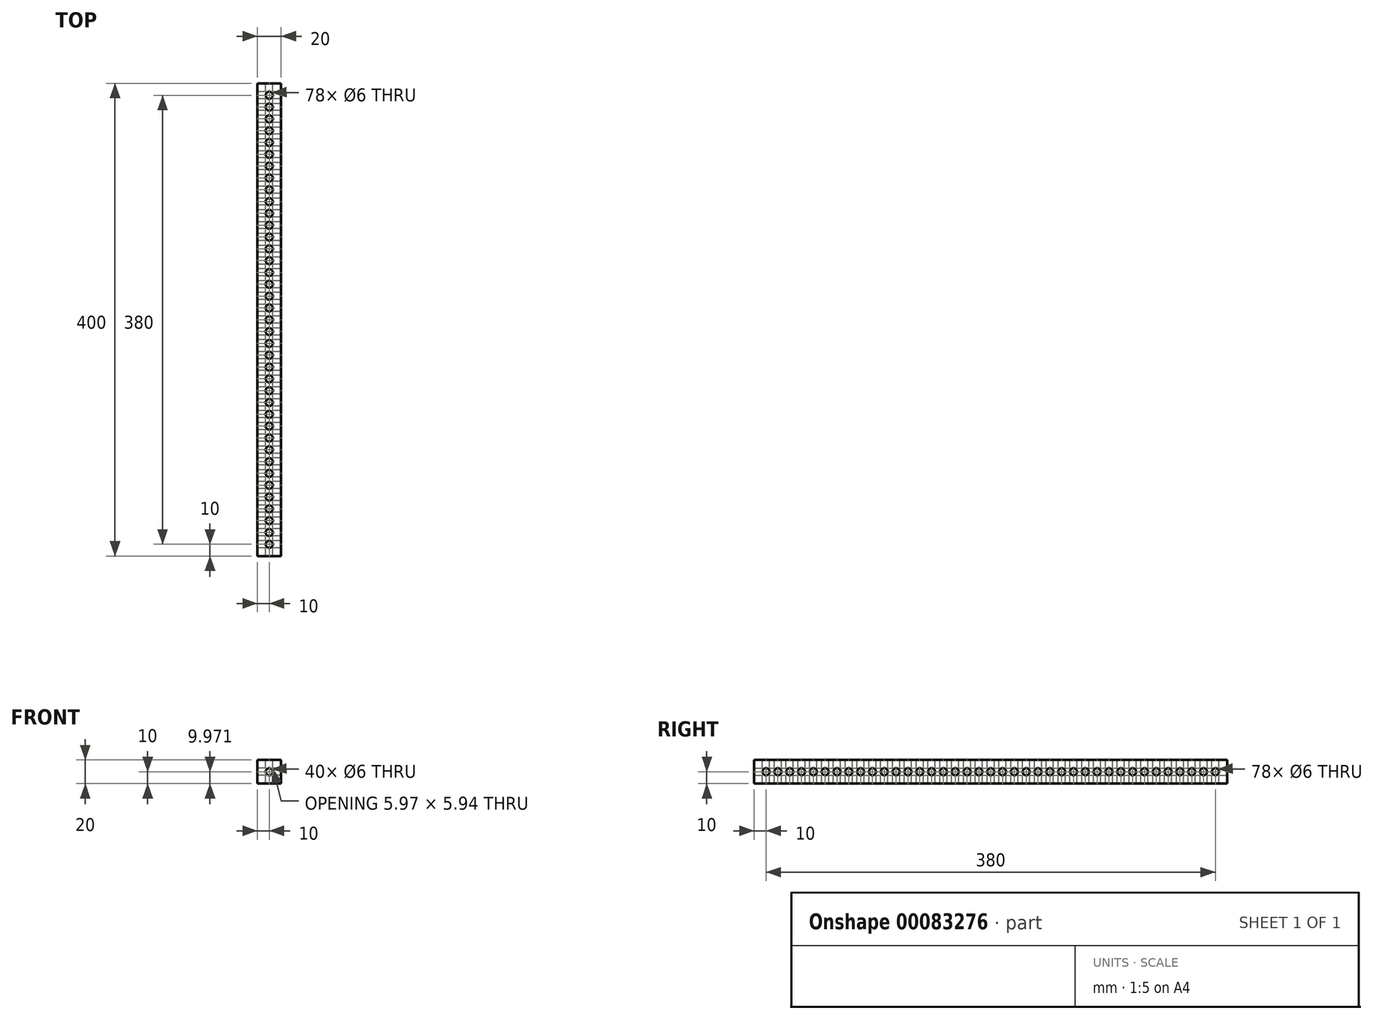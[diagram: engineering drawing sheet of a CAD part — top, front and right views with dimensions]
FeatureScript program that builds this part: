
annotation { "Feature Type Name" : "Feature", "Feature Type Description" : "" }
export const myFeature = defineFeature(function(context is Context, id is Id, definition is map)
    precondition{}
    {
        {
            var Q0;
            Q0=qCreatedBy(makeId("Front.planeOp"),FACE);
            var sketch = newSketch(context, id + "F0", { "sketchPlane" : qUnion([Q0])});
            skLineSegment(sketch, "E0.bottom", {"start": v(10, 10) * mm, "end": v(-10, 10) * mm});
            skLineSegment(sketch, "E0.top", {"start": v(10, -10) * mm, "end": v(-10, -10) * mm});
            skLineSegment(sketch, "E0.left", {"start": v(10, 10) * mm, "end": v(10, -10) * mm});
            skLineSegment(sketch, "E0.right", {"start": v(-10, 10) * mm, "end": v(-10, -10) * mm});
            skPoint(sketch, "E0.middle", {"position": v(0, 0) * mm});
            skCircle(sketch, "E1", {"center": v(0, 0) * mm, "radius": 3 * mm});
            skSolve(sketch);
        }
        {
            var Q0;
            Q0 = qSketchRegion(id + "F0", true);
            extrude(context, id + "F1", {"entities" : qUnion([Q0]), "depth" : 400 * mm});
        }
        {
            var Q0;
            Q0=makeQuery(id+"F1.opExtrude","SWEPT_FACE",FACE,{"disambiguationData":[OSD([sQuery(id+"F0.wireOp",EDGE,"E0.bottom")])]});
            var sketch = newSketch(context, id + "F2", { "sketchPlane" : qUnion([Q0])});
            skCircle(sketch, "E2", {"center": v(0, -10) * mm, "radius": 3 * mm});
            skCircle(sketch, "E3.0.1.0", {"center": v(0, -20) * mm, "radius": 3 * mm});
            skCircle(sketch, "E3.0.2.0", {"center": v(0, -30) * mm, "radius": 3 * mm});
            skCircle(sketch, "E3.0.3.0", {"center": v(0, -40) * mm, "radius": 3 * mm});
            skCircle(sketch, "E3.0.4.0", {"center": v(0, -50) * mm, "radius": 3 * mm});
            skCircle(sketch, "E3.0.5.0", {"center": v(0, -60) * mm, "radius": 3 * mm});
            skCircle(sketch, "E3.0.6.0", {"center": v(0, -70) * mm, "radius": 3 * mm});
            skCircle(sketch, "E3.0.7.0", {"center": v(0, -80) * mm, "radius": 3 * mm});
            skCircle(sketch, "E3.0.8.0", {"center": v(0, -90) * mm, "radius": 3 * mm});
            skCircle(sketch, "E3.0.9.0", {"center": v(0, -100) * mm, "radius": 3 * mm});
            skCircle(sketch, "E3.0.10.0", {"center": v(0, -110) * mm, "radius": 3 * mm});
            skCircle(sketch, "E3.0.11.0", {"center": v(0, -120) * mm, "radius": 3 * mm});
            skCircle(sketch, "E3.0.12.0", {"center": v(0, -130) * mm, "radius": 3 * mm});
            skCircle(sketch, "E3.0.13.0", {"center": v(0, -140) * mm, "radius": 3 * mm});
            skCircle(sketch, "E3.0.14.0", {"center": v(0, -150) * mm, "radius": 3 * mm});
            skCircle(sketch, "E3.0.15.0", {"center": v(0, -160) * mm, "radius": 3 * mm});
            skCircle(sketch, "E3.0.16.0", {"center": v(0, -170) * mm, "radius": 3 * mm});
            skCircle(sketch, "E3.0.17.0", {"center": v(0, -180) * mm, "radius": 3 * mm});
            skCircle(sketch, "E3.0.18.0", {"center": v(0, -190) * mm, "radius": 3 * mm});
            skCircle(sketch, "E3.0.19.0", {"center": v(0, -200) * mm, "radius": 3 * mm});
            skCircle(sketch, "E3.0.20.0", {"center": v(0, -210) * mm, "radius": 3 * mm});
            skCircle(sketch, "E3.0.21.0", {"center": v(0, -220) * mm, "radius": 3 * mm});
            skCircle(sketch, "E3.0.22.0", {"center": v(0, -230) * mm, "radius": 3 * mm});
            skCircle(sketch, "E3.0.23.0", {"center": v(0, -240) * mm, "radius": 3 * mm});
            skCircle(sketch, "E3.0.24.0", {"center": v(0, -250) * mm, "radius": 3 * mm});
            skCircle(sketch, "E3.0.25.0", {"center": v(0, -260) * mm, "radius": 3 * mm});
            skCircle(sketch, "E3.0.26.0", {"center": v(0, -270) * mm, "radius": 3 * mm});
            skCircle(sketch, "E3.0.27.0", {"center": v(0, -280) * mm, "radius": 3 * mm});
            skCircle(sketch, "E3.0.28.0", {"center": v(0, -290) * mm, "radius": 3 * mm});
            skCircle(sketch, "E3.0.29.0", {"center": v(0, -300) * mm, "radius": 3 * mm});
            skCircle(sketch, "E3.0.30.0", {"center": v(0, -310) * mm, "radius": 3 * mm});
            skCircle(sketch, "E3.0.31.0", {"center": v(0, -320) * mm, "radius": 3 * mm});
            skCircle(sketch, "E3.0.32.0", {"center": v(0, -330) * mm, "radius": 3 * mm});
            skCircle(sketch, "E3.0.33.0", {"center": v(0, -340) * mm, "radius": 3 * mm});
            skCircle(sketch, "E3.0.34.0", {"center": v(0, -350) * mm, "radius": 3 * mm});
            skCircle(sketch, "E3.0.35.0", {"center": v(0, -360) * mm, "radius": 3 * mm});
            skCircle(sketch, "E3.0.36.0", {"center": v(0, -370) * mm, "radius": 3 * mm});
            skCircle(sketch, "E3.0.37.0", {"center": v(0, -380) * mm, "radius": 3 * mm});
            skCircle(sketch, "E3.0.38.0", {"center": v(0, -390) * mm, "radius": 3 * mm});
            skLineSegment(sketch, "E3.direction1", {"start": v(0, -10) * mm, "end": v(25, -10) * mm, "construction": true});
            skLineSegment(sketch, "E3.direction2", {"start": v(0, -10) * mm, "end": v(0, -20) * mm, "construction": true});
            skSolve(sketch);
        }
        {
            var Q0;
            Q0 = qSketchRegion(id + "F2", true);
            extrude(context, id + "F3", {"entities" : qUnion([Q0]), "operationType" : NewBodyOperationType.REMOVE, "endBound" : BoundingType.THROUGH_ALL, "oppositeDirection" : true, "depth" : 25 * mm});
        }
        {
            var Q0;
            Q0=makeQuery(id+"F1.opExtrude","SWEPT_FACE",FACE,{"disambiguationData":[OSD([sQuery(id+"F0.wireOp",EDGE,"E0.right")])]});
            var sketch = newSketch(context, id + "F4", { "sketchPlane" : qUnion([Q0])});
            skCircle(sketch, "E4", {"center": v(10, 0) * mm, "radius": 3 * mm});
            skCircle(sketch, "E5.1.0.0", {"center": v(20, 0) * mm, "radius": 3 * mm});
            skCircle(sketch, "E5.2.0.0", {"center": v(30, 0) * mm, "radius": 3 * mm});
            skCircle(sketch, "E5.3.0.0", {"center": v(40, 0) * mm, "radius": 3 * mm});
            skCircle(sketch, "E5.4.0.0", {"center": v(50, 0) * mm, "radius": 3 * mm});
            skCircle(sketch, "E5.5.0.0", {"center": v(60, 0) * mm, "radius": 3 * mm});
            skCircle(sketch, "E5.6.0.0", {"center": v(70, 0) * mm, "radius": 3 * mm});
            skCircle(sketch, "E5.7.0.0", {"center": v(80, 0) * mm, "radius": 3 * mm});
            skCircle(sketch, "E5.8.0.0", {"center": v(90, 0) * mm, "radius": 3 * mm});
            skCircle(sketch, "E5.9.0.0", {"center": v(100, 0) * mm, "radius": 3 * mm});
            skCircle(sketch, "E5.10.0.0", {"center": v(110, 0) * mm, "radius": 3 * mm});
            skCircle(sketch, "E5.11.0.0", {"center": v(120, 0) * mm, "radius": 3 * mm});
            skCircle(sketch, "E5.12.0.0", {"center": v(130, 0) * mm, "radius": 3 * mm});
            skCircle(sketch, "E5.13.0.0", {"center": v(140, 0) * mm, "radius": 3 * mm});
            skCircle(sketch, "E5.14.0.0", {"center": v(150, 0) * mm, "radius": 3 * mm});
            skCircle(sketch, "E5.15.0.0", {"center": v(160, 0) * mm, "radius": 3 * mm});
            skCircle(sketch, "E5.16.0.0", {"center": v(170, 0) * mm, "radius": 3 * mm});
            skCircle(sketch, "E5.17.0.0", {"center": v(180, 0) * mm, "radius": 3 * mm});
            skCircle(sketch, "E5.18.0.0", {"center": v(190, 0) * mm, "radius": 3 * mm});
            skCircle(sketch, "E5.19.0.0", {"center": v(200, 0) * mm, "radius": 3 * mm});
            skCircle(sketch, "E5.20.0.0", {"center": v(210, 0) * mm, "radius": 3 * mm});
            skCircle(sketch, "E5.21.0.0", {"center": v(220, 0) * mm, "radius": 3 * mm});
            skCircle(sketch, "E5.22.0.0", {"center": v(230, 0) * mm, "radius": 3 * mm});
            skCircle(sketch, "E5.23.0.0", {"center": v(240, 0) * mm, "radius": 3 * mm});
            skCircle(sketch, "E5.24.0.0", {"center": v(250, 0) * mm, "radius": 3 * mm});
            skCircle(sketch, "E5.25.0.0", {"center": v(260, 0) * mm, "radius": 3 * mm});
            skCircle(sketch, "E5.26.0.0", {"center": v(270, 0) * mm, "radius": 3 * mm});
            skCircle(sketch, "E5.27.0.0", {"center": v(280, 0) * mm, "radius": 3 * mm});
            skCircle(sketch, "E5.28.0.0", {"center": v(290, 0) * mm, "radius": 3 * mm});
            skCircle(sketch, "E5.29.0.0", {"center": v(300, 0) * mm, "radius": 3 * mm});
            skCircle(sketch, "E5.30.0.0", {"center": v(310, 0) * mm, "radius": 3 * mm});
            skCircle(sketch, "E5.31.0.0", {"center": v(320, 0) * mm, "radius": 3 * mm});
            skCircle(sketch, "E5.32.0.0", {"center": v(330, 0) * mm, "radius": 3 * mm});
            skCircle(sketch, "E5.33.0.0", {"center": v(340, 0) * mm, "radius": 3 * mm});
            skCircle(sketch, "E5.34.0.0", {"center": v(350, 0) * mm, "radius": 3 * mm});
            skCircle(sketch, "E5.35.0.0", {"center": v(360, 0) * mm, "radius": 3 * mm});
            skCircle(sketch, "E5.36.0.0", {"center": v(370, 0) * mm, "radius": 3 * mm});
            skCircle(sketch, "E5.37.0.0", {"center": v(380, 0) * mm, "radius": 3 * mm});
            skCircle(sketch, "E5.38.0.0", {"center": v(390, 0) * mm, "radius": 3 * mm});
            skLineSegment(sketch, "E5.direction1", {"start": v(10, 0) * mm, "end": v(20, 0) * mm, "construction": true});
            skSolve(sketch);
        }
        {
            var Q0;
            Q0 = qSketchRegion(id + "F4", true);
            extrude(context, id + "F5", {"entities" : qUnion([Q0]), "operationType" : NewBodyOperationType.REMOVE, "endBound" : BoundingType.THROUGH_ALL, "oppositeDirection" : true, "depth" : 25 * mm});
        }
    });
